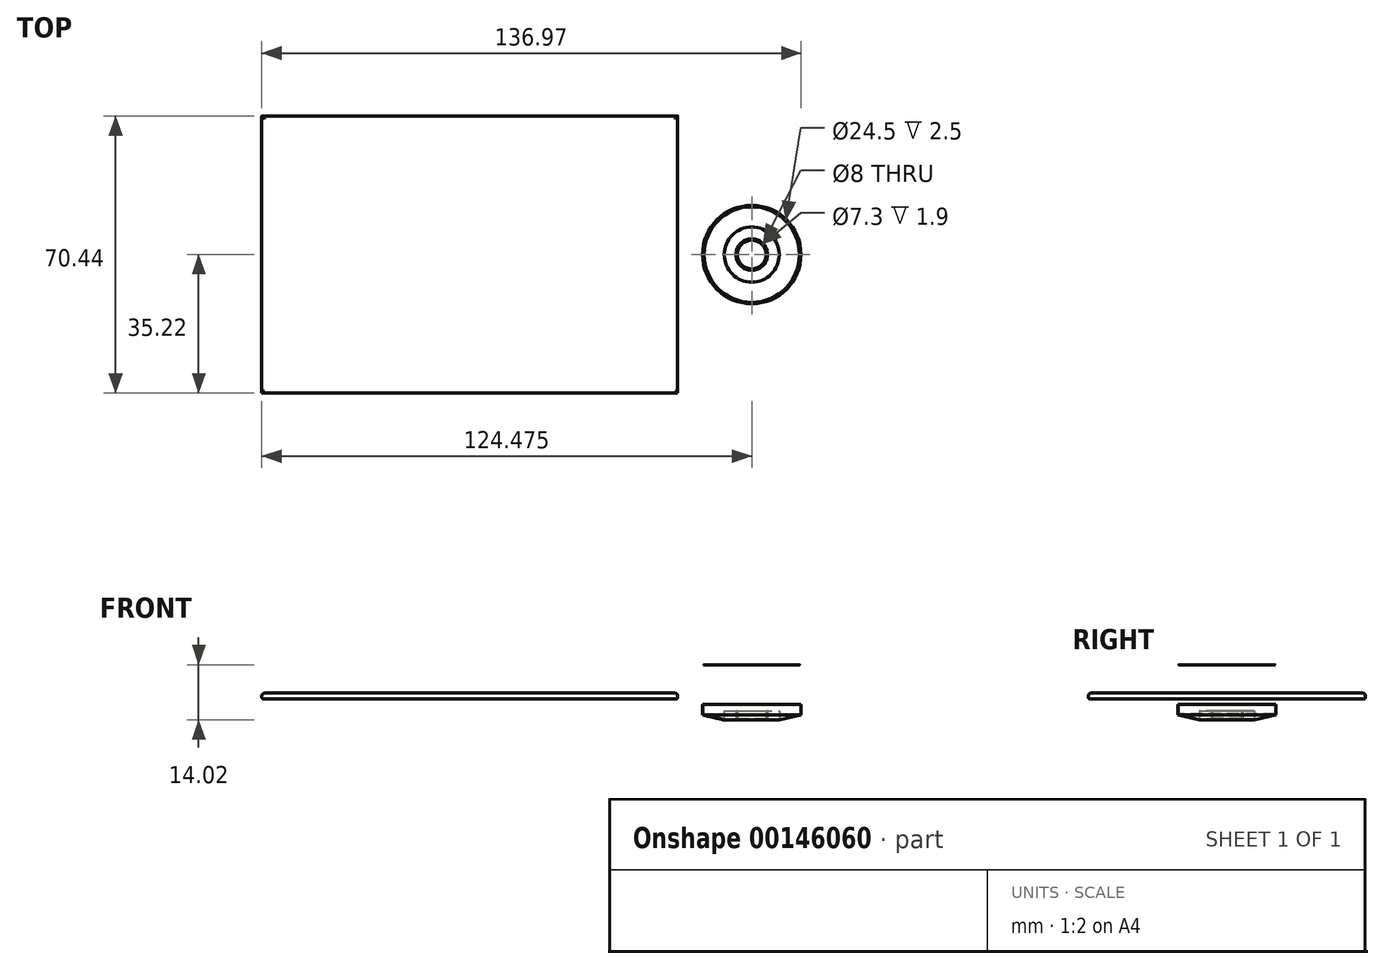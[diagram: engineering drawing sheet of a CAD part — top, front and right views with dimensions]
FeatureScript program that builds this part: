
annotation { "Feature Type Name" : "Feature", "Feature Type Description" : "" }
export const myFeature = defineFeature(function(context is Context, id is Id, definition is map)
    precondition{}
    {
        {
            var Q0;
            Q0=qCreatedBy(makeId("Top.planeOp"),FACE);
            var sketch = newSketch(context, id + "F0", { "sketchPlane" : qUnion([Q0])});
            skLineSegment(sketch, "E0.bottom", {"start": v(52.84, 35.22) * mm, "end": v(-52.84, 35.22) * mm});
            skLineSegment(sketch, "E0.top", {"start": v(52.84, -35.22) * mm, "end": v(-52.84, -35.22) * mm});
            skLineSegment(sketch, "E0.left", {"start": v(52.84, 35.22) * mm, "end": v(52.84, -35.22) * mm});
            skLineSegment(sketch, "E0.right", {"start": v(-52.84, 35.22) * mm, "end": v(-52.84, -35.22) * mm});
            skPoint(sketch, "E0.middle", {"position": v(0, 0) * mm});
            skSolve(sketch);
        }
        {
            var Q0;
            Q0=makeQuery(id+"F0.imprint","IMPRINT",FACE,{"disambiguationData":[TD([[makeQuery(id+"F0.imprint","IMPRINT",EDGE,{"derivedFrom":sQuery(id+"F0.wireOp",EDGE,"E0.bottom")}),1.0]])]});
            extrude(context, id + "F9", {"entities" : qUnion([Q0]), "depth" : 1.5 * mm});
        }
        {
            var Q0;
            Q0=makeQuery(id+"F9.opExtrude","CAP_EDGE",EDGE,{"disambiguationData":[OSD([sQuery(id+"F0.wireOp",EDGE,"E0.top")])],"isStart":true});
            var Q1;
            Q1=makeQuery(id+"F9.opExtrude","CAP_EDGE",EDGE,{"disambiguationData":[OSD([sQuery(id+"F0.wireOp",EDGE,"E0.right")])],"isStart":true});
            var Q2;
            Q2=makeQuery(id+"F9.opExtrude","CAP_EDGE",EDGE,{"disambiguationData":[OSD([sQuery(id+"F0.wireOp",EDGE,"E0.bottom")])],"isStart":true});
            var Q3;
            Q3=makeQuery(id+"F9.opExtrude","CAP_EDGE",EDGE,{"disambiguationData":[OSD([sQuery(id+"F0.wireOp",EDGE,"E0.left")])],"isStart":true});
            fillet(context, id + "F1", {"entities" : qUnion([Q0, Q1, Q2, Q3]), "radius" : 0.5 * mm, "tangentPropagation" : true, "allowEdgeOverflow" : false});
        }
        {
            var Q0;
            Q0=makeQuery(id+"F9.opExtrude","CAP_EDGE",EDGE,{"disambiguationData":[OSD([sQuery(id+"F0.wireOp",EDGE,"E0.left")])],"isStart":false});
            var Q1;
            Q1=makeQuery(id+"F9.opExtrude","CAP_EDGE",EDGE,{"disambiguationData":[OSD([sQuery(id+"F0.wireOp",EDGE,"E0.bottom")])],"isStart":false});
            var Q2;
            Q2=makeQuery(id+"F9.opExtrude","CAP_EDGE",EDGE,{"disambiguationData":[OSD([sQuery(id+"F0.wireOp",EDGE,"E0.right")])],"isStart":false});
            var Q3;
            Q3=makeQuery(id+"F9.opExtrude","CAP_EDGE",EDGE,{"disambiguationData":[OSD([sQuery(id+"F0.wireOp",EDGE,"E0.top")])],"isStart":false});
            fillet(context, id + "F2", {"entities" : qUnion([Q0, Q1, Q2, Q3]), "radius" : 0.75 * mm, "tangentPropagation" : true, "allowEdgeOverflow" : false});
        }
        {
            var Q0;
            Q0=qCreatedBy(makeId("Front.planeOp"),FACE);
            var sketch = newSketch(context, id + "F3", { "sketchPlane" : qUnion([Q0])});
            skLineSegment(sketch, "E1.bottom", {"start": v(71.63, 4.68) * mm, "end": v(84.13, 4.68) * mm});
            skLineSegment(sketch, "E1.top", {"start": v(71.63, 8.68) * mm, "end": v(84.13, 8.68) * mm});
            skLineSegment(sketch, "E1.left", {"start": v(71.63, 4.68) * mm, "end": v(71.63, 8.68) * mm, "construction": true});
            skLineSegment(sketch, "E1.right", {"start": v(84.13, 4.68) * mm, "end": v(84.13, 8.68) * mm});
            skLineSegment(sketch, "E2", {"start": v(83.88, 8.68) * mm, "end": v(83.88, 6.18) * mm});
            skLineSegment(sketch, "E3", {"start": v(71.63, 4.93) * mm, "end": v(78.63, 4.93) * mm});
            skLineSegment(sketch, "E4", {"start": v(83.88, 6.18) * mm, "end": v(78.63, 4.93) * mm});
            skLineSegment(sketch, "E5", {"start": v(78.66, 4.68) * mm, "end": v(84.13, 5.98) * mm});
            skLineSegment(sketch, "E6", {"start": v(78.63, 4.93) * mm, "end": v(78.63, 6.93) * mm});
            skLineSegment(sketch, "E7", {"start": v(78.63, 6.93) * mm, "end": v(75.63, 6.93) * mm});
            skLineSegment(sketch, "E8", {"start": v(75.63, 6.93) * mm, "end": v(75.63, 4.93) * mm});
            skLineSegment(sketch, "E9.bottom", {"start": v(75.53, 5.03) * mm, "end": v(75.28, 5.03) * mm});
            skLineSegment(sketch, "E9.top", {"start": v(75.53, 6.93) * mm, "end": v(75.28, 6.93) * mm});
            skLineSegment(sketch, "E9.left", {"start": v(75.53, 5.03) * mm, "end": v(75.53, 6.93) * mm});
            skLineSegment(sketch, "E9.right", {"start": v(75.28, 5.03) * mm, "end": v(75.28, 6.93) * mm});
            skFitSpline(sketch, "E10", {"points": [v(71.63, 7.2) * mm, v(75.56, 7.01) * mm, v(75.59, 6.93) * mm], "startDerivative": vector(6.22, 0.2) * mm, "endDerivative": vector(0.06, -0.45) * mm});
            skFitSpline(sketch, "E11", {"points": [v(75.59, 6.93) * mm, v(75.6, 7.01) * mm, v(83.77, 7.64) * mm], "startDerivative": vector(0.02, 0.6) * mm, "endDerivative": vector(12.73, 0.7) * mm});
            skFitSpline(sketch, "E12", {"points": [v(83.88, 8.68) * mm, v(83.77, 8.68) * mm, v(83.77, 7.64) * mm], "startDerivative": vector(-1.3, 0) * mm, "endDerivative": vector(0.18, -1.93) * mm});
            skArc(sketch, "E13.filletArc", {"start": v(83.74, 7.64) * mm, "mid": v(83.76, 7.65) * mm, "end": v(83.76, 7.66) * mm});
            skLineSegment(sketch, "E14", {"start": v(78.63, 4.94) * mm, "end": v(75.63, 4.94) * mm});
            skLineSegment(sketch, "E15", {"start": v(71.63, 4.68) * mm, "end": v(71.63, 4.93) * mm});
            skArc(sketch, "E16.filletArc", {"start": v(75.56, 7) * mm, "mid": v(75.58, 7) * mm, "end": v(75.6, 7) * mm});
            skFitSpline(sketch, "E17.0", {"points": [v(71.63, 7.21) * mm, v(72.15, 7.23) * mm, v(72.94, 7.24) * mm, v(73.9, 7.23) * mm, v(74.53, 7.2) * mm, v(75.04, 7.16) * mm, v(75.41, 7.1) * mm, v(75.6, 7.02) * mm, v(75.6, 6.94) * mm, v(75.6, 6.93) * mm]});
            skFitSpline(sketch, "E18.0", {"points": [v(75.58, 6.93) * mm, v(75.58, 6.94) * mm, v(75.57, 6.97) * mm, v(75.6, 7.02) * mm, v(75.66, 7.06) * mm, v(75.8, 7.11) * mm, v(76.15, 7.18) * mm, v(76.8, 7.26) * mm, v(77.86, 7.34) * mm, v(79.16, 7.42) * mm, v(81.1, 7.51) * mm, v(82.7, 7.59) * mm, v(83.77, 7.65) * mm]});
            skFitSpline(sketch, "E19.0", {"points": [v(83.88, 8.69) * mm, v(83.86, 8.69) * mm, v(83.82, 8.7) * mm, v(83.8, 8.7) * mm, v(83.78, 8.7) * mm, v(83.77, 8.7) * mm, v(83.76, 8.69) * mm, v(83.76, 8.68) * mm, v(83.75, 8.66) * mm, v(83.75, 8.6) * mm, v(83.74, 8.45) * mm, v(83.73, 8.12) * mm, v(83.74, 7.8) * mm, v(83.76, 7.64) * mm]});
            skArc(sketch, "E20.filletArc", {"start": v(83.73, 7.65) * mm, "mid": v(83.75, 7.65) * mm, "end": v(83.75, 7.67) * mm});
            skArc(sketch, "E21.filletArc", {"start": v(75.57, 7.02) * mm, "mid": v(75.58, 7.01) * mm, "end": v(75.6, 7.02) * mm});
            skLineSegment(sketch, "E22", {"start": v(71.63, 7.2) * mm, "end": v(71.63, 7.21) * mm});
            skLineSegment(sketch, "E23", {"start": v(83.88, 8.68) * mm, "end": v(83.88, 8.69) * mm});
            skSolve(sketch);
        }
        {
            var Q0;
            {var subQ0=sQuery(id+"F3.wireOp",EDGE,"E2");Q0=makeQuery(id+"F3.imprint","IMPRINT",FACE,{"disambiguationData":[TD([[makeQuery(id+"F3.imprint","IMPRINT",EDGE,{"derivedFrom":subQ0}),1.0]])]});}
            var Q1;
            Q1=sQuery(id+"F3.wireOp",EDGE,"E1.left");
            revolve(context, id + "F4", {"entities" : qUnion([Q0]), "axis" : qUnion([Q1]), "revolveType" : RevolveType.FULL});
        }
        {
            var Q0;
            {var subQ0=sQuery(id+"F3.wireOp",EDGE,"E7");Q0=makeQuery(id+"F3.imprint","IMPRINT",FACE,{"disambiguationData":[TD([[makeQuery(id+"F3.imprint","IMPRINT",EDGE,{"derivedFrom":subQ0}),1.0]])]});}
            var Q1;
            Q1=sQuery(id+"F3.wireOp",EDGE,"E1.left");
            revolve(context, id + "F5", {"entities" : qUnion([Q0]), "axis" : qUnion([Q1]), "revolveType" : RevolveType.FULL});
        }
        {
            var Q0;
            Q0=makeQuery(id+"F3.imprint","IMPRINT",FACE,{"disambiguationData":[TD([[makeQuery(id+"F3.imprint","IMPRINT",EDGE,{"derivedFrom":sQuery(id+"F3.wireOp",EDGE,"E9.bottom")}),-1.0]])]});
            var Q1;
            Q1=sQuery(id+"F3.wireOp",EDGE,"E1.left");
            revolve(context, id + "F6", {"entities" : qUnion([Q0]), "axis" : qUnion([Q1]), "revolveType" : RevolveType.FULL});
        }
        {
            var Q0;
            {var subQ5=sQuery(id+"F3.wireOp",EDGE,"E23");Q0=makeQuery(id+"F3.imprint","IMPRINT",FACE,{"disambiguationData":[TD([[makeQuery(id+"F3.imprint","IMPRINT",EDGE,{"derivedFrom":subQ5}),1.0]])]});}
            var Q1;
            Q1=makeQuery(id+"F3.imprint","IMPRINT",FACE,{"disambiguationData":[TD([[makeQuery(id+"F3.imprint","IMPRINT",EDGE,{"derivedFrom":sQuery(id+"F3.wireOp",EDGE,"E10")}),1.0]])]});
            var Q2;
            Q2=sQuery(id+"F3.wireOp",EDGE,"E10");
            var Q3;
            Q3=sQuery(id+"F3.wireOp",EDGE,"E11");
            var Q4;
            Q4=sQuery(id+"F3.wireOp",EDGE,"E12");
            var Q5;
            Q5=sQuery(id+"F3.wireOp",EDGE,"E13.filletArc");
            var Q6;
            Q6=sQuery(id+"F3.wireOp",EDGE,"E1.left");
            revolve(context, id + "F7", {"entities" : qUnion([Q0, Q1]), "surfaceEntities" : qUnion([Q2, Q3, Q4, Q5]), "axis" : qUnion([Q6]), "revolveType" : RevolveType.FULL});
        }
        {
            var Q0;
            Q0=makeQuery(id+"F4.opRevolve","SWEPT_BODY",BODY,{"disambiguationData":[OSD([sQuery(id+"F3.wireOp",EDGE,"E1.bottom"),sQuery(id+"F3.wireOp",EDGE,"E1.top"),sQuery(id+"F3.wireOp",EDGE,"E1.right"),sQuery(id+"F3.wireOp",EDGE,"E2"),sQuery(id+"F3.wireOp",EDGE,"E3"),sQuery(id+"F3.wireOp",EDGE,"E4"),sQuery(id+"F3.wireOp",EDGE,"E5"),sQuery(id+"F3.wireOp",EDGE,"E15")])]});
            var Q1;
            Q1=makeQuery(id+"F7.opRevolve","SWEPT_BODY",BODY,{"disambiguationData":[OSD([sQuery(id+"F3.wireOp",EDGE,"E10"),sQuery(id+"F3.wireOp",EDGE,"E11"),sQuery(id+"F3.wireOp",EDGE,"E12"),sQuery(id+"F3.wireOp",EDGE,"E13.filletArc"),sQuery(id+"F3.wireOp",EDGE,"E16.filletArc"),sQuery(id+"F3.wireOp",EDGE,"E17.0"),sQuery(id+"F3.wireOp",EDGE,"E18.0"),sQuery(id+"F3.wireOp",EDGE,"E19.0"),sQuery(id+"F3.wireOp",EDGE,"E20.filletArc"),sQuery(id+"F3.wireOp",EDGE,"E21.filletArc"),sQuery(id+"F3.wireOp",EDGE,"E22"),sQuery(id+"F3.wireOp",EDGE,"E23")])]});
            var Q2;
            Q2=makeQuery(id+"F5.opRevolve","SWEPT_BODY",BODY,{"disambiguationData":[OSD([sQuery(id+"F3.wireOp",EDGE,"E6"),sQuery(id+"F3.wireOp",EDGE,"E7"),sQuery(id+"F3.wireOp",EDGE,"E8"),sQuery(id+"F3.wireOp",EDGE,"E14")])]});
            var Q3;
            Q3=makeQuery(id+"F6.opRevolve","SWEPT_BODY",BODY,{"disambiguationData":[OSD([sQuery(id+"F3.wireOp",EDGE,"E9.bottom"),sQuery(id+"F3.wireOp",EDGE,"E9.top"),sQuery(id+"F3.wireOp",EDGE,"E9.left"),sQuery(id+"F3.wireOp",EDGE,"E9.right")])]});
            transform(context, id + "F8", {"entities" : qUnion([Q0, Q1, Q2, Q3]), "transformType" : TransformType.TRANSLATION_3D, "dx" : 0 * mm, "dy" : 0 * mm, "dz" : -10 * mm, "makeCopy" : false});
        }
    });
